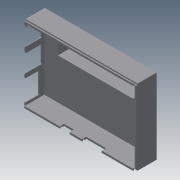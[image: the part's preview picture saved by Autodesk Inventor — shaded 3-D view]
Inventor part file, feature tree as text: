
AUTODESK INVENTOR PART (.ipt)
format: ipt  version: 2015 (Build 190159000, 159)  size: 287,744 bytes
history: native  units: in
note: dims shown in document units (in); Inventor stores cm internally (conversion verified against a paired STEP export)
features: extrude x17, sketch x17
ambient origin geometry x8: Origin, YZ Plane, XZ Plane, XY Plane, X Axis, Y Axis, Z Axis, Center Point
bodies: Solid1 (feature_tree)
feature tree (34):
  extrude  "Extrusion1"  Depth=2.4016in
  extrude  "Extrusion2"  Depth=0.0591in
  extrude  "Extrusion3"  Depth=0.0591in
  extrude  "Extrusion4"  Depth=0.6299in TaperAngle=0.0deg
  extrude  "Extrusion5"  Depth=0.4724in
  extrude  "Extrusion6"  Depth=0.1378in
  extrude  "Extrusion7"  Depth=0.5512in
  extrude  "Extrusion8"  Depth=0.1772in
  extrude  "Extrusion9"  Depth=0.0394in TaperAngle=0.0deg
  extrude  "Extrusion10"  Depth=0.3543in
  extrude  "Extrusion11"  Depth=0.0591in
  extrude  "Extrusion12"  Depth=2.4016in
  extrude  "Extrusion13"  Depth=0.6299in TaperAngle=0.0deg
  extrude  "Extrusion14"  Depth=0.0394in
  extrude  "Extrusion15"  Depth=0.0394in
  extrude  "Extrusion16"  Depth=0.0394in
  extrude  "Extrusion17"  Depth=0.0197in
  sketch  "Sketch1"  dims[d0=3.563in d1=2.4016in]
  sketch  "Sketch2"  dims[d2=0.0591in d3=0.0in d4=0.0591in]
  sketch  "Sketch3"  dims[d5=0.0591in d6=0.0591in]
  sketch  "Sketch4"  dims[d7=0.0394in d8=0.6299in d9=0.0in]
  sketch  "Sketch5"  dims[d10=0.1378in d11=0.4724in]
  sketch  "Sketch6"  dims[d12=0.6693in d13=0.1378in]
  sketch  "Sketch7"  dims[d14=0.5512in d15=0.5512in]
  sketch  "Sketch8"  dims[d16=0.5512in d17=0.1772in]
  sketch  "Sketch9"  dims[d18=0.5512in d19=0.0394in d20=0.0in]
  sketch  "Sketch10"  dims[d21=2.4016in d22=0.3543in]
  sketch  "Sketch11"  dims[d23=0.0591in d24=0.0in d25=0.0591in]
  sketch  "Sketch12"  dims[d26=0.0591in d28=2.4016in]
  sketch  "Sketch13"  dims[d29=0.3543in d30=0.6299in d31=0.0in]
  sketch  "Sketch14"  dims[d32=0.1378in d33=0.0394in]
  sketch  "Sketch15"  dims[d34=0.0197in d35=0.0394in]
  sketch  "Sketch16"  dims[d36=0.4724in d37=0.0in d38=0.0394in]
  sketch  "Sketch17"  dims[d39=0.4724in d40=0.0in d41=0.0197in d42=0.0394in d43=0.0394in d44=0.4724in d45=0.0in d46=0.0394in d47=0.0197in d48=0.4724in d49=0.0in d50=1.1614in d51=0.315in d53=0.6299in d57=0.3937in d59=0.0591in d60=0.0in d61=0.0433in d62=0.0354in d63=0.0433in d64=0.0354in d65=0.0433in d66=0.0354in d67=0.0394in d68=0.0in d69=0.0433in d70=0.0354in d71=0.0394in d72=0.0in d73=0.0394in d74=0.0in d75=0.0394in d76=0.0in d77=0.0394in d78=0.0in d79=0.0394in d80=0.0in d81=2.4016in d82=0.0394in d83=0.0in d84=0.0669in]
